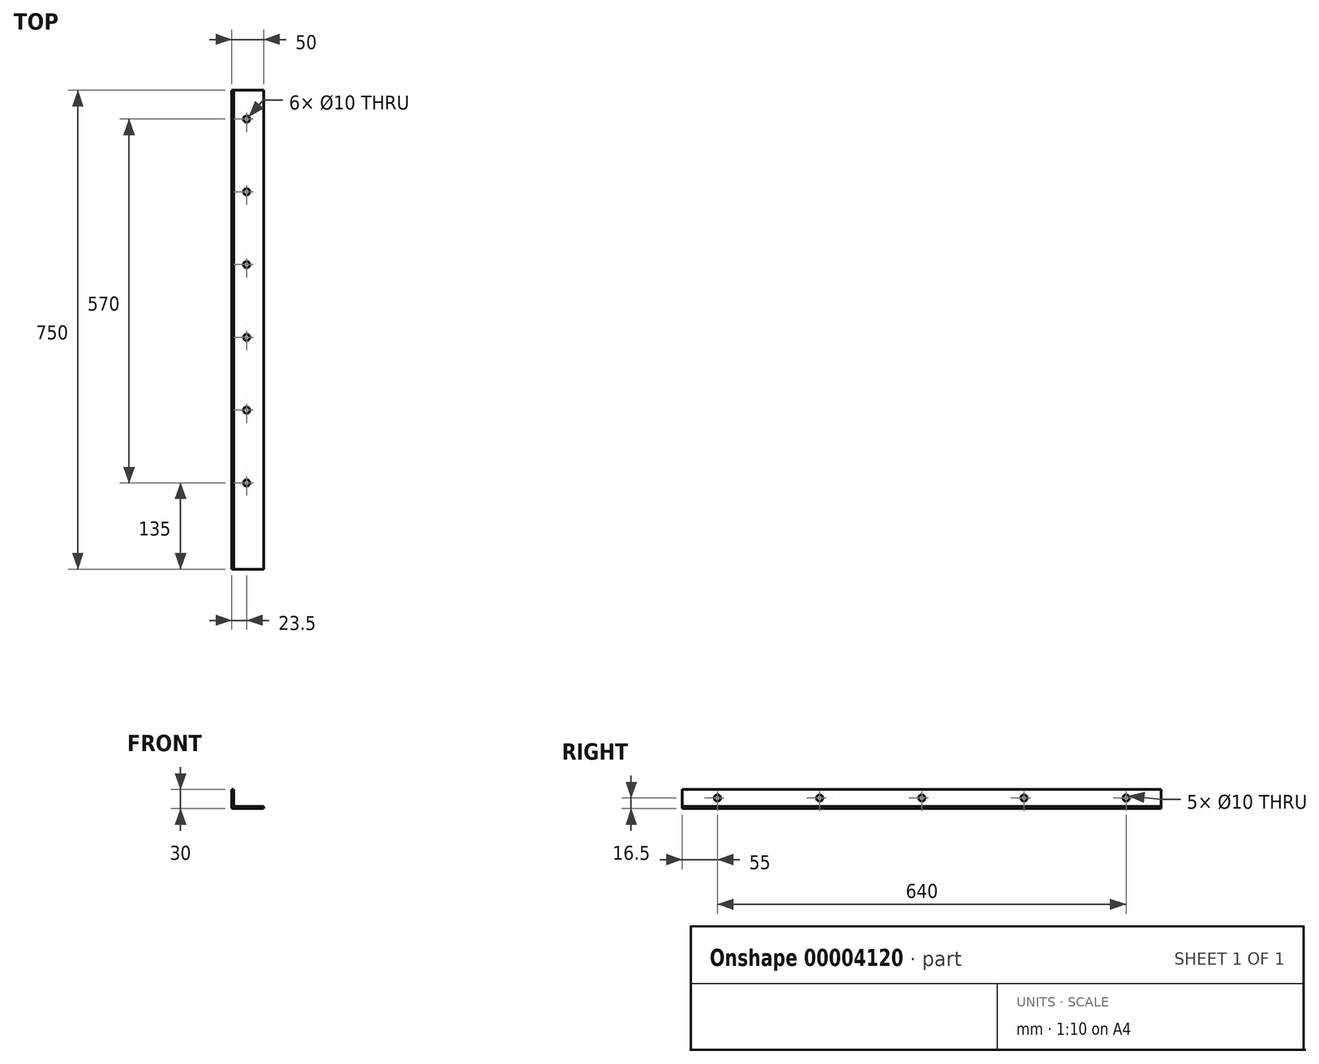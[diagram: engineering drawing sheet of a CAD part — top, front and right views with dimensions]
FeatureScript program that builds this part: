
annotation { "Feature Type Name" : "Feature", "Feature Type Description" : "" }
export const myFeature = defineFeature(function(context is Context, id is Id, definition is map)
    precondition{}
    {
        {
            var Q0;
            Q0=qCreatedBy(makeId("Front.planeOp"),FACE);
            var sketch = newSketch(context, id + "F0", { "sketchPlane" : qUnion([Q0])});
            skLineSegment(sketch, "E0", {"start": v(0, 0) * mm, "end": v(0, 30) * mm});
            skLineSegment(sketch, "E1", {"start": v(0, 30) * mm, "end": v(3, 30) * mm});
            skLineSegment(sketch, "E2", {"start": v(3, 30) * mm, "end": v(3, 3) * mm});
            skLineSegment(sketch, "E3", {"start": v(3, 3) * mm, "end": v(50, 3) * mm});
            skLineSegment(sketch, "E4", {"start": v(50, 3) * mm, "end": v(50, 0) * mm});
            skLineSegment(sketch, "E5", {"start": v(50, 0) * mm, "end": v(0, 0) * mm});
            skSolve(sketch);
        }
        {
            var Q0;
            Q0=makeQuery(id+"F0.imprint","IMPRINT",FACE,{"disambiguationData":[TD([[makeQuery(id+"F0.imprint","IMPRINT",EDGE,{"derivedFrom":sQuery(id+"F0.wireOp",EDGE,"E0")}),-1.0]])]});
            extrude(context, id + "F1", {"entities" : qUnion([Q0]), "depth" : 750 * mm});
        }
        {
            var Q0;
            Q0=makeQuery(id+"F1.opExtrude","SWEPT_FACE",FACE,{"disambiguationData":[OSD([sQuery(id+"F0.wireOp",EDGE,"E2")])]});
            var sketch = newSketch(context, id + "F2", { "sketchPlane" : qUnion([Q0])});
            skLineSegment(sketch, "E6", {"start": v(-750, 16.5) * mm, "end": v(0, 16.5) * mm});
            skCircle(sketch, "E7", {"center": v(-695, 16.5) * mm, "radius": 5 * mm});
            skCircle(sketch, "E8.1.0.0", {"center": v(-535, 16.5) * mm, "radius": 5 * mm});
            skCircle(sketch, "E8.2.0.0", {"center": v(-375, 16.5) * mm, "radius": 5 * mm});
            skCircle(sketch, "E8.3.0.0", {"center": v(-215, 16.5) * mm, "radius": 5 * mm});
            skCircle(sketch, "E8.4.0.0", {"center": v(-55, 16.5) * mm, "radius": 5 * mm});
            skLineSegment(sketch, "E8.direction1", {"start": v(-695, 16.5) * mm, "end": v(-535, 16.5) * mm, "construction": true});
            skSolve(sketch);
        }
        {
            var Q0;
            {var subQ0=sQuery(id+"F2.wireOp",EDGE,"E7");var subQ1=sQuery(id+"F2.wireOp",EDGE,"E6");var subQ3=makeQuery(id+"F2.imprint","INTERSECT",VERTEX,{"disambiguationData":[OD(0.0)],"derivedFrom":[subQ1,subQ0]});Q0=makeQuery(id+"F2.imprint","IMPRINT",FACE,{"disambiguationData":[TD([[makeQuery(id+"F2.imprint","IMPRINT",EDGE,{"disambiguationData":[TD([[subQ3,-1.0]])],"derivedFrom":subQ1}),-1.0]])]});}
            var Q1;
            {var subQ0=sQuery(id+"F2.wireOp",EDGE,"E7");var subQ1=sQuery(id+"F2.wireOp",EDGE,"E6");var subQ3=makeQuery(id+"F2.imprint","INTERSECT",VERTEX,{"disambiguationData":[OD(0.0)],"derivedFrom":[subQ1,subQ0]});Q1=makeQuery(id+"F2.imprint","IMPRINT",FACE,{"disambiguationData":[TD([[makeQuery(id+"F2.imprint","IMPRINT",EDGE,{"disambiguationData":[TD([[subQ3,-1.0]])],"derivedFrom":subQ1}),1.0]])]});}
            var Q2;
            {var subQ0=sQuery(id+"F2.wireOp",EDGE,"E8.1.0.0");var subQ1=sQuery(id+"F2.wireOp",EDGE,"E6");var subQ3=makeQuery(id+"F2.imprint","INTERSECT",VERTEX,{"disambiguationData":[OD(0.0)],"derivedFrom":[subQ1,subQ0]});Q2=makeQuery(id+"F2.imprint","IMPRINT",FACE,{"disambiguationData":[TD([[makeQuery(id+"F2.imprint","IMPRINT",EDGE,{"disambiguationData":[TD([[subQ3,-1.0]])],"derivedFrom":subQ1}),-1.0]])]});}
            var Q3;
            {var subQ0=sQuery(id+"F2.wireOp",EDGE,"E8.1.0.0");var subQ1=sQuery(id+"F2.wireOp",EDGE,"E6");var subQ3=makeQuery(id+"F2.imprint","INTERSECT",VERTEX,{"disambiguationData":[OD(0.0)],"derivedFrom":[subQ1,subQ0]});Q3=makeQuery(id+"F2.imprint","IMPRINT",FACE,{"disambiguationData":[TD([[makeQuery(id+"F2.imprint","IMPRINT",EDGE,{"disambiguationData":[TD([[subQ3,-1.0]])],"derivedFrom":subQ1}),1.0]])]});}
            var Q4;
            {var subQ0=sQuery(id+"F2.wireOp",EDGE,"E8.2.0.0");var subQ1=sQuery(id+"F2.wireOp",EDGE,"E6");var subQ3=makeQuery(id+"F2.imprint","INTERSECT",VERTEX,{"disambiguationData":[OD(0.0)],"derivedFrom":[subQ1,subQ0]});Q4=makeQuery(id+"F2.imprint","IMPRINT",FACE,{"disambiguationData":[TD([[makeQuery(id+"F2.imprint","IMPRINT",EDGE,{"disambiguationData":[TD([[subQ3,-1.0]])],"derivedFrom":subQ1}),-1.0]])]});}
            var Q5;
            {var subQ0=sQuery(id+"F2.wireOp",EDGE,"E8.2.0.0");var subQ1=sQuery(id+"F2.wireOp",EDGE,"E6");var subQ3=makeQuery(id+"F2.imprint","INTERSECT",VERTEX,{"disambiguationData":[OD(0.0)],"derivedFrom":[subQ1,subQ0]});Q5=makeQuery(id+"F2.imprint","IMPRINT",FACE,{"disambiguationData":[TD([[makeQuery(id+"F2.imprint","IMPRINT",EDGE,{"disambiguationData":[TD([[subQ3,-1.0]])],"derivedFrom":subQ1}),1.0]])]});}
            var Q6;
            {var subQ0=sQuery(id+"F2.wireOp",EDGE,"E8.3.0.0");var subQ1=sQuery(id+"F2.wireOp",EDGE,"E6");var subQ3=makeQuery(id+"F2.imprint","INTERSECT",VERTEX,{"disambiguationData":[OD(0.0)],"derivedFrom":[subQ1,subQ0]});Q6=makeQuery(id+"F2.imprint","IMPRINT",FACE,{"disambiguationData":[TD([[makeQuery(id+"F2.imprint","IMPRINT",EDGE,{"disambiguationData":[TD([[subQ3,-1.0]])],"derivedFrom":subQ1}),-1.0]])]});}
            var Q7;
            {var subQ0=sQuery(id+"F2.wireOp",EDGE,"E8.3.0.0");var subQ1=sQuery(id+"F2.wireOp",EDGE,"E6");var subQ3=makeQuery(id+"F2.imprint","INTERSECT",VERTEX,{"disambiguationData":[OD(0.0)],"derivedFrom":[subQ1,subQ0]});Q7=makeQuery(id+"F2.imprint","IMPRINT",FACE,{"disambiguationData":[TD([[makeQuery(id+"F2.imprint","IMPRINT",EDGE,{"disambiguationData":[TD([[subQ3,-1.0]])],"derivedFrom":subQ1}),1.0]])]});}
            var Q8;
            {var subQ0=sQuery(id+"F2.wireOp",EDGE,"E8.4.0.0");var subQ1=sQuery(id+"F2.wireOp",EDGE,"E6");var subQ3=makeQuery(id+"F2.imprint","INTERSECT",VERTEX,{"disambiguationData":[OD(0.0)],"derivedFrom":[subQ1,subQ0]});Q8=makeQuery(id+"F2.imprint","IMPRINT",FACE,{"disambiguationData":[TD([[makeQuery(id+"F2.imprint","IMPRINT",EDGE,{"disambiguationData":[TD([[subQ3,-1.0]])],"derivedFrom":subQ1}),-1.0]])]});}
            var Q9;
            {var subQ0=sQuery(id+"F2.wireOp",EDGE,"E8.4.0.0");var subQ1=sQuery(id+"F2.wireOp",EDGE,"E6");var subQ3=makeQuery(id+"F2.imprint","INTERSECT",VERTEX,{"disambiguationData":[OD(0.0)],"derivedFrom":[subQ1,subQ0]});Q9=makeQuery(id+"F2.imprint","IMPRINT",FACE,{"disambiguationData":[TD([[makeQuery(id+"F2.imprint","IMPRINT",EDGE,{"disambiguationData":[TD([[subQ3,-1.0]])],"derivedFrom":subQ1}),1.0]])]});}
            extrude(context, id + "F3", {"entities" : qUnion([Q0, Q1, Q2, Q3, Q4, Q5, Q6, Q7, Q8, Q9]), "operationType" : NewBodyOperationType.REMOVE, "oppositeDirection" : true, "depth" : 25 * mm});
        }
        {
            var Q0;
            Q0=makeQuery(id+"F1.opExtrude","SWEPT_FACE",FACE,{"disambiguationData":[OSD([sQuery(id+"F0.wireOp",EDGE,"E3")])]});
            var sketch = newSketch(context, id + "F4", { "sketchPlane" : qUnion([Q0])});
            skLineSegment(sketch, "E9", {"start": v(23.5, -750) * mm, "end": v(23.5, 0) * mm});
            skCircle(sketch, "E10", {"center": v(23.5, -615) * mm, "radius": 5 * mm});
            skCircle(sketch, "E11.0.1.0", {"center": v(23.5, -501) * mm, "radius": 5 * mm});
            skCircle(sketch, "E11.0.2.0", {"center": v(23.5, -387) * mm, "radius": 5 * mm});
            skCircle(sketch, "E11.0.3.0", {"center": v(23.5, -273) * mm, "radius": 5 * mm});
            skCircle(sketch, "E11.0.4.0", {"center": v(23.5, -159) * mm, "radius": 5 * mm});
            skCircle(sketch, "E11.0.5.0", {"center": v(23.5, -45) * mm, "radius": 5 * mm});
            skLineSegment(sketch, "E11.direction1", {"start": v(23.5, -615) * mm, "end": v(47.5, -615) * mm, "construction": true});
            skLineSegment(sketch, "E11.direction2", {"start": v(23.5, -615) * mm, "end": v(23.5, -501) * mm, "construction": true});
            skSolve(sketch);
        }
        {
            var Q0;
            {var subQ0=sQuery(id+"F4.wireOp",EDGE,"E11.0.5.0");var subQ1=sQuery(id+"F4.wireOp",EDGE,"E9");var subQ3=makeQuery(id+"F4.imprint","INTERSECT",VERTEX,{"disambiguationData":[OD(0.0)],"derivedFrom":[subQ1,subQ0]});Q0=makeQuery(id+"F4.imprint","IMPRINT",FACE,{"disambiguationData":[TD([[makeQuery(id+"F4.imprint","IMPRINT",EDGE,{"disambiguationData":[TD([[subQ3,-1.0]])],"derivedFrom":subQ1}),1.0]])]});}
            var Q1;
            {var subQ0=sQuery(id+"F4.wireOp",EDGE,"E11.0.5.0");var subQ1=sQuery(id+"F4.wireOp",EDGE,"E9");var subQ3=makeQuery(id+"F4.imprint","INTERSECT",VERTEX,{"disambiguationData":[OD(0.0)],"derivedFrom":[subQ1,subQ0]});Q1=makeQuery(id+"F4.imprint","IMPRINT",FACE,{"disambiguationData":[TD([[makeQuery(id+"F4.imprint","IMPRINT",EDGE,{"disambiguationData":[TD([[subQ3,-1.0]])],"derivedFrom":subQ1}),-1.0]])]});}
            var Q2;
            {var subQ0=sQuery(id+"F4.wireOp",EDGE,"E11.0.4.0");var subQ1=sQuery(id+"F4.wireOp",EDGE,"E9");var subQ3=makeQuery(id+"F4.imprint","INTERSECT",VERTEX,{"disambiguationData":[OD(0.0)],"derivedFrom":[subQ1,subQ0]});Q2=makeQuery(id+"F4.imprint","IMPRINT",FACE,{"disambiguationData":[TD([[makeQuery(id+"F4.imprint","IMPRINT",EDGE,{"disambiguationData":[TD([[subQ3,-1.0]])],"derivedFrom":subQ1}),-1.0]])]});}
            var Q3;
            {var subQ0=sQuery(id+"F4.wireOp",EDGE,"E11.0.4.0");var subQ1=sQuery(id+"F4.wireOp",EDGE,"E9");var subQ3=makeQuery(id+"F4.imprint","INTERSECT",VERTEX,{"disambiguationData":[OD(0.0)],"derivedFrom":[subQ1,subQ0]});Q3=makeQuery(id+"F4.imprint","IMPRINT",FACE,{"disambiguationData":[TD([[makeQuery(id+"F4.imprint","IMPRINT",EDGE,{"disambiguationData":[TD([[subQ3,-1.0]])],"derivedFrom":subQ1}),1.0]])]});}
            var Q4;
            {var subQ0=sQuery(id+"F4.wireOp",EDGE,"E11.0.3.0");var subQ1=sQuery(id+"F4.wireOp",EDGE,"E9");var subQ3=makeQuery(id+"F4.imprint","INTERSECT",VERTEX,{"disambiguationData":[OD(0.0)],"derivedFrom":[subQ1,subQ0]});Q4=makeQuery(id+"F4.imprint","IMPRINT",FACE,{"disambiguationData":[TD([[makeQuery(id+"F4.imprint","IMPRINT",EDGE,{"disambiguationData":[TD([[subQ3,-1.0]])],"derivedFrom":subQ1}),1.0]])]});}
            var Q5;
            {var subQ0=sQuery(id+"F4.wireOp",EDGE,"E11.0.3.0");var subQ1=sQuery(id+"F4.wireOp",EDGE,"E9");var subQ3=makeQuery(id+"F4.imprint","INTERSECT",VERTEX,{"disambiguationData":[OD(0.0)],"derivedFrom":[subQ1,subQ0]});Q5=makeQuery(id+"F4.imprint","IMPRINT",FACE,{"disambiguationData":[TD([[makeQuery(id+"F4.imprint","IMPRINT",EDGE,{"disambiguationData":[TD([[subQ3,-1.0]])],"derivedFrom":subQ1}),-1.0]])]});}
            var Q6;
            {var subQ0=sQuery(id+"F4.wireOp",EDGE,"E11.0.2.0");var subQ1=sQuery(id+"F4.wireOp",EDGE,"E9");var subQ3=makeQuery(id+"F4.imprint","INTERSECT",VERTEX,{"disambiguationData":[OD(0.0)],"derivedFrom":[subQ1,subQ0]});Q6=makeQuery(id+"F4.imprint","IMPRINT",FACE,{"disambiguationData":[TD([[makeQuery(id+"F4.imprint","IMPRINT",EDGE,{"disambiguationData":[TD([[subQ3,-1.0]])],"derivedFrom":subQ1}),-1.0]])]});}
            var Q7;
            {var subQ0=sQuery(id+"F4.wireOp",EDGE,"E11.0.2.0");var subQ1=sQuery(id+"F4.wireOp",EDGE,"E9");var subQ3=makeQuery(id+"F4.imprint","INTERSECT",VERTEX,{"disambiguationData":[OD(0.0)],"derivedFrom":[subQ1,subQ0]});Q7=makeQuery(id+"F4.imprint","IMPRINT",FACE,{"disambiguationData":[TD([[makeQuery(id+"F4.imprint","IMPRINT",EDGE,{"disambiguationData":[TD([[subQ3,-1.0]])],"derivedFrom":subQ1}),1.0]])]});}
            var Q8;
            {var subQ0=sQuery(id+"F4.wireOp",EDGE,"E11.0.1.0");var subQ1=sQuery(id+"F4.wireOp",EDGE,"E9");var subQ3=makeQuery(id+"F4.imprint","INTERSECT",VERTEX,{"disambiguationData":[OD(0.0)],"derivedFrom":[subQ1,subQ0]});Q8=makeQuery(id+"F4.imprint","IMPRINT",FACE,{"disambiguationData":[TD([[makeQuery(id+"F4.imprint","IMPRINT",EDGE,{"disambiguationData":[TD([[subQ3,-1.0]])],"derivedFrom":subQ1}),1.0]])]});}
            var Q9;
            {var subQ0=sQuery(id+"F4.wireOp",EDGE,"E11.0.1.0");var subQ1=sQuery(id+"F4.wireOp",EDGE,"E9");var subQ3=makeQuery(id+"F4.imprint","INTERSECT",VERTEX,{"disambiguationData":[OD(0.0)],"derivedFrom":[subQ1,subQ0]});Q9=makeQuery(id+"F4.imprint","IMPRINT",FACE,{"disambiguationData":[TD([[makeQuery(id+"F4.imprint","IMPRINT",EDGE,{"disambiguationData":[TD([[subQ3,-1.0]])],"derivedFrom":subQ1}),-1.0]])]});}
            var Q10;
            {var subQ0=sQuery(id+"F4.wireOp",EDGE,"E10");var subQ1=sQuery(id+"F4.wireOp",EDGE,"E9");var subQ3=makeQuery(id+"F4.imprint","INTERSECT",VERTEX,{"disambiguationData":[OD(0.0)],"derivedFrom":[subQ1,subQ0]});Q10=makeQuery(id+"F4.imprint","IMPRINT",FACE,{"disambiguationData":[TD([[makeQuery(id+"F4.imprint","IMPRINT",EDGE,{"disambiguationData":[TD([[subQ3,-1.0]])],"derivedFrom":subQ1}),1.0]])]});}
            var Q11;
            {var subQ0=sQuery(id+"F4.wireOp",EDGE,"E10");var subQ1=sQuery(id+"F4.wireOp",EDGE,"E9");var subQ3=makeQuery(id+"F4.imprint","INTERSECT",VERTEX,{"disambiguationData":[OD(0.0)],"derivedFrom":[subQ1,subQ0]});Q11=makeQuery(id+"F4.imprint","IMPRINT",FACE,{"disambiguationData":[TD([[makeQuery(id+"F4.imprint","IMPRINT",EDGE,{"disambiguationData":[TD([[subQ3,-1.0]])],"derivedFrom":subQ1}),-1.0]])]});}
            extrude(context, id + "F5", {"entities" : qUnion([Q0, Q1, Q2, Q3, Q4, Q5, Q6, Q7, Q8, Q9, Q10, Q11]), "operationType" : NewBodyOperationType.REMOVE, "oppositeDirection" : true, "depth" : 25 * mm});
        }
    });
